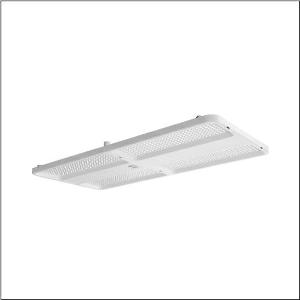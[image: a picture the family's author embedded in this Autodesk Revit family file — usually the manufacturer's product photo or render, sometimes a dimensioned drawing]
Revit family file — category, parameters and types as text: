
# Revit family: highbay_21_maxi_52hn11db4qda01
name_source: partatom
category: Lighting Fixtures
units: mm (PartAtom-declared; Revit-internal decimal feet)

## family parameters
Cut with Voids When Loaded = No
Host = Face
Light Source = No
Part Type = Normal
Room Calculation Point = No
Round Connector Dimension = Use Diameter
Shared = No

## types (1)
- --- (1 x LED, 38000 lm, 198.2 W, 4000K)
    Apparent Load = 198 VA
    CIE Flux Codes = 89 97 99 100 100
    Color Rendering = 80
    Color Temperature = 4000K
    Default Elevation = 1800 mm
    Description = high bay luminaire Highbay 21 maxi; direct symmetric narrow distribution, light control with lens of PMMA; UGR ≤ 19 (X = 4H | Y = 8H | S = 0.25H | reflection values 70/50/20); luminous flux: 38.000lm; light colour: 840, colour temperature: 4000K, MacAdam ≤ 3 SDCM (initial), colour rendering: CRI > 80; luminous efficacy: 191,7lm/W; rated service life: 75.000h (L80) at AT= ta max; control: Bluetooth Mesh; for wireless networking: Node multi-sensor luminaire for setting up a local control solution without a higher-level application controller, intelligence completely integrated into the luminaire; with auto-swarm function: leading lighting creates safety. The function is already active without any „out-of-the-box“ commissioning; commissioning is not necessary thanks to „out-of-the-box“ functions: basic functions (presence lighting, follow-up times, fading times, etc.) are already preset at the factory; no control line such as DALI between the Node multi-sensor luminaires and Nodes is required, wireless integration of other Node luminaires and Node multi-sensor luminaires into the network is possible; number of Node multi-sensor luminaires in the project can be expanded as required, network sizes > 300 Nodes can be realized; can also be connected to lighting or building automation via various gateways upon request; integrated DALI2 ECG provides luminaire data (according to IEC62386, Part 251), energy data (Part 252), and monitoring and analytics data (Part 253) to higher-level systems for further processing; luminaire with PIR sensor (passive-infrared); with light sensor; luminaire connection: terminal, 5-pole, max. 2.5mm² (cable entry for one cable, Ø 8.5..16mm); mains connection: 230..240V, AC 50/60Hz; connected load: 198,2W; protection rating (complete): IP65; insulation class (complete): insulation class I (protective earthing); protection symbol: D; certification: CE, UKCA; internal wiring halogen-free; luminaire LABS conformity tested according to VDMA 24364:2018-05; Suitable for use in the food industry according to the specifications of IFS-Food, HACCP and/or BRC; housing frame of high-performance plastic PA6, matt traffic white (RAL 9016); cover of PMMA; dimension (LxWxH): 946 x 442 x 72mm; permissible operating ambient temperature: -20..+40°C (reducing of maximum allowable ambient temperature of 5°C with ceiling mounting); packaging unit: 1 piece; (delivery without accessories; please order mounting accessories separately)
    Height = 72 mm  [stored 0.23622 ft]
    Lamp = 1 x LED
    Lamp Light Flux = 38000 lm
    Lamp Power = 198.2 W
    Lamp count = 1
    Length = 946 mm
    Luminous efficacy = 192 lm/W
    Manufacturer = Siteco
    ModVariant = No
    Model = 52HN11DB4QDA01
    Mounting Place = Ceiling
    Mounting Type = Pendant
    Number of Poles = 1
    OnlyDefault = Yes
    Power Factor = 1
    Product Name = Highbay 21 maxi
    Product group = high bay luminaire
    ProductGroupID = 902
    Protection Class = Protection class I
    Protection Degree = IP 65
    RLX_Detail_Level = 1
    RLX_Emergency_Light_Flux = 0 lm
    RLX_Emergency_Type = 0
    RLX_Emergency_Type_DB = No
    RlxData = <blob elided: 129137 chars, md5=cf196779>
    Socket = socket
    Standby Power = 0 W
    System Light Flux = 38001 lm
    System Power = 198 W
    Type Comments = factory setting: luminous flux: 100 % | dim-lin: 254 | 918 mA
    Type Image = l_1363267.jpg
    URL = http://relux.com
    VarID = @adj_012743
    Voltage = 0 V
    Weight = 0.00 kg
    Width = 442 mm

note: [stored X ft] marks values corroborated as IEEE doubles in the binary element streams (Revit-internal decimal feet)

## geometry (parser evidence)
native form markers: Blend x4, Sweep x10
no freeform markers — native parametric forms only
